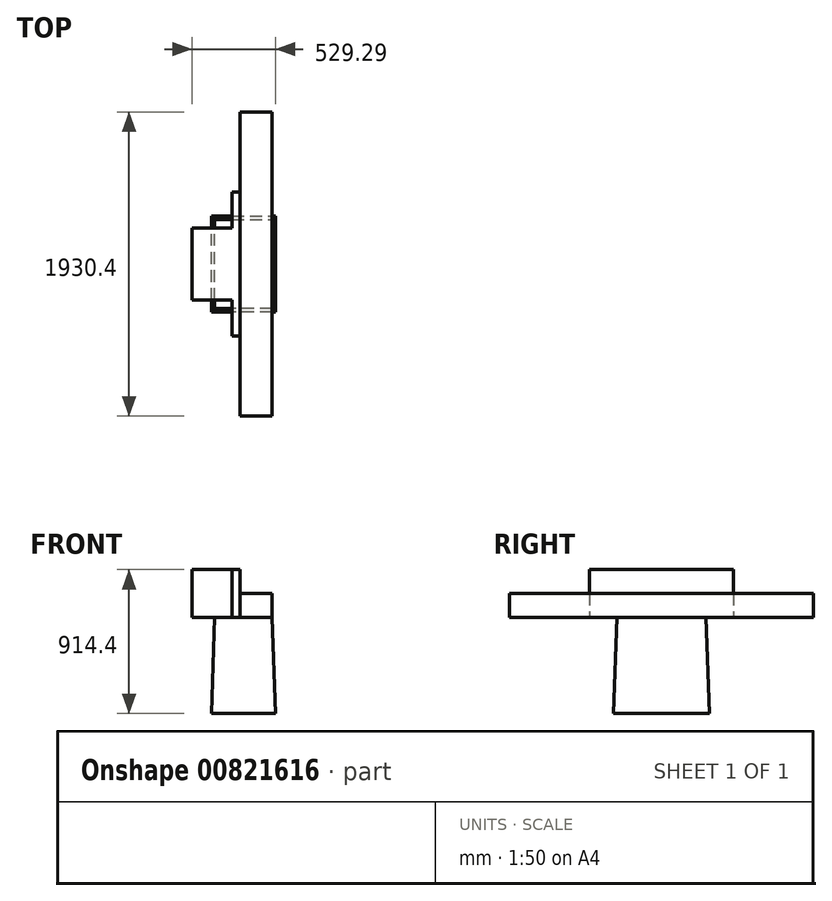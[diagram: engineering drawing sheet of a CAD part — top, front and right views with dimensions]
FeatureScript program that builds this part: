
annotation { "Feature Type Name" : "Feature", "Feature Type Description" : "" }
export const myFeature = defineFeature(function(context is Context, id is Id, definition is map)
    precondition{}
    {
        {
            var Q0;
            Q0=qCreatedBy(makeId("Top.planeOp"),FACE);
            var sketch = newSketch(context, id + "F0", { "sketchPlane" : qUnion([Q0])});
            skLineSegment(sketch, "E0.bottom", {"start": v(0, 0) * mm, "end": v(406.4, 0) * mm});
            skLineSegment(sketch, "E0.top", {"start": v(0, 609.6) * mm, "end": v(406.4, 609.6) * mm});
            skLineSegment(sketch, "E0.left", {"start": v(0, 0) * mm, "end": v(0, 609.6) * mm});
            skLineSegment(sketch, "E0.right", {"start": v(406.4, 0) * mm, "end": v(406.4, 609.6) * mm});
            skSolve(sketch);
        }
        {
            var Q0;
            Q0 = qSketchRegion(id + "F0", true);
            extrude(context, id + "F1", {"entities" : qUnion([Q0]), "depth" : 609.6 * mm, "offsetDistance" : 25.4 * mm, "hasDraft" : true, "draftAngle" : 2 * degree, "draftPullDirection" : true});
        }
        {
            var Q0;
            Q0=makeQuery(id+"F1.opExtrude","CAP_FACE",FACE,{"disambiguationData":[OSD([sQuery(id+"F0.wireOp",EDGE,"E0.bottom"),sQuery(id+"F0.wireOp",EDGE,"E0.top"),sQuery(id+"F0.wireOp",EDGE,"E0.left"),sQuery(id+"F0.wireOp",EDGE,"E0.right")])],"isStart":false});
            var sketch = newSketch(context, id + "F2", { "sketchPlane" : qUnion([Q0])});
            skLineSegment(sketch, "E1.bottom", {"start": v(181.91, -660.4) * mm, "end": v(385.11, -660.4) * mm});
            skLineSegment(sketch, "E1.top", {"start": v(181.91, 1270) * mm, "end": v(385.11, 1270) * mm});
            skLineSegment(sketch, "E1.left", {"start": v(181.91, -660.4) * mm, "end": v(181.91, 1270) * mm});
            skLineSegment(sketch, "E1.right", {"start": v(385.11, -660.4) * mm, "end": v(385.11, 1270) * mm});
            skSolve(sketch);
        }
        {
            var Q0;
            Q0 = qSketchRegion(id + "F2", true);
            extrude(context, id + "F3", {"entities" : qUnion([Q0]), "operationType" : NewBodyOperationType.ADD, "depth" : 152.4 * mm, "offsetDistance" : 25.4 * mm});
        }
        {
            var Q0;
            Q0=makeQuery(id+"F1.opExtrude","CAP_FACE",FACE,{"disambiguationData":[OSD([sQuery(id+"F0.wireOp",EDGE,"E0.bottom"),sQuery(id+"F0.wireOp",EDGE,"E0.top"),sQuery(id+"F0.wireOp",EDGE,"E0.left"),sQuery(id+"F0.wireOp",EDGE,"E0.right")])],"isStart":false});
            var sketch = newSketch(context, id + "F4", { "sketchPlane" : qUnion([Q0])});
            skLineSegment(sketch, "E2", {"start": v(181.91, 762) * mm, "end": v(131.11, 762) * mm});
            skLineSegment(sketch, "E3", {"start": v(131.11, 762) * mm, "end": v(131.11, 533.4) * mm});
            skLineSegment(sketch, "E4", {"start": v(131.11, 533.4) * mm, "end": v(-122.89, 533.4) * mm});
            skLineSegment(sketch, "E5", {"start": v(-122.89, 533.4) * mm, "end": v(-122.89, 76.2) * mm});
            skLineSegment(sketch, "E6", {"start": v(-122.89, 76.2) * mm, "end": v(131.11, 76.2) * mm});
            skLineSegment(sketch, "E7", {"start": v(131.11, 76.2) * mm, "end": v(131.11, -152.4) * mm});
            skLineSegment(sketch, "E8", {"start": v(131.11, -152.4) * mm, "end": v(181.91, -152.4) * mm});
            skLineSegment(sketch, "E9", {"start": v(181.91, -152.4) * mm, "end": v(181.91, 762) * mm});
            skSolve(sketch);
        }
        {
            var Q0;
            Q0 = qSketchRegion(id + "F4", true);
            extrude(context, id + "F5", {"entities" : qUnion([Q0]), "operationType" : NewBodyOperationType.ADD, "depth" : 304.8 * mm, "offsetDistance" : 25.4 * mm});
        }
    });
